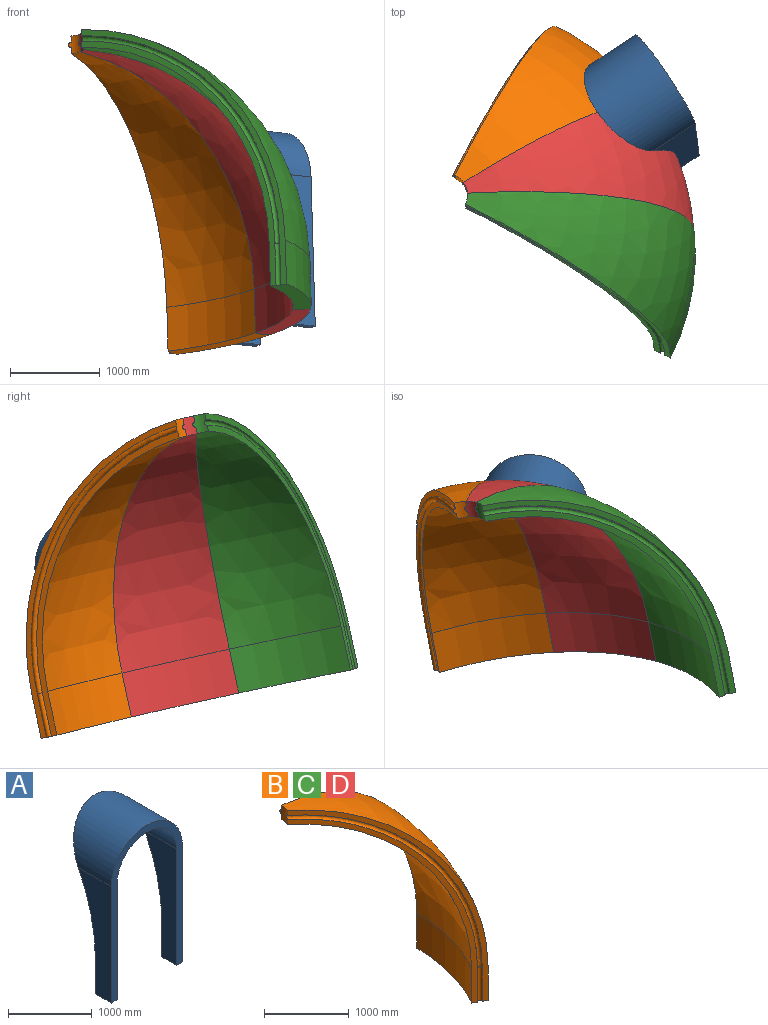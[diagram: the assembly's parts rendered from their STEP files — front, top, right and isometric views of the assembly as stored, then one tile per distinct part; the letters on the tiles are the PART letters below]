
ASSEMBLY  parts=4 mates=7
PART A: 12 faces, bbox 1350.7x951.5x2300 mm
  f0: plane 267.51x100mm, normal (0,0,-1), area 25677.6mm2, adj f1,f7,f8,f9
  f1: plane 1700x533.57mm, normal (1,0,0), area 531535.4mm2, adj f0,f2,f8,f9,f11
  f2: cylinder r=500mm len=1000mm, axis (0,-1,0), area 1103442.8mm2, adj f1,f3,f8,f11
  f3: plane 1700x533.57mm, normal (-1,0,0), area 531535.4mm2, adj f2,f4,f8,f10,f11
  f4: plane 267.51x100mm, normal (0,0,-1), area 25677.6mm2, adj f3,f5,f8,f10
  f5: plane 1700x556.93mm, normal (1,0,0), area 567862.4mm2, adj f4,f6,f8,f10,f11
  f6: cylinder r=600mm len=1200mm, axis (0,-1,0), area 1440019.9mm2, adj f5,f7,f8,f11
  f7: plane 1700x556.93mm, normal (-1,0,0), area 567862.4mm2, adj f0,f6,f8,f9,f11
  f8: plane 2300x1200mm, normal (0,-1,0), area 512787.6mm2, adj f0,f1,f2,f3,f4,f5,f6,f7
  f9: cylinder r=2700mm len=500mm, axis (0,0,-1), area 51074.3mm2, adj f0,f1,f7,f11
  f10: cylinder r=2700mm len=500mm, axis (0,0,-1), area 51074.3mm2, adj f3,f4,f5,f11
  f11: sphere r=2700mm, area 470269.1mm2, adj f1,f2,f3,f5,f6,f7,f9,f10
PART B: 14 faces, bbox 2700x1410x3188.4 mm
  f0: plane 3058.19x2009.8mm, normal (-0.5,-0.87,0), area 296399mm2, adj f4,f7,f8,f9,f12,f13
  f1: bspline ~2635.58x2630.01mm, area 361903.8mm2, adj f2,f6,f11,f13
  f2: plane 3060.29x2320.13mm, normal (0,1,0), area 301979.9mm2, adj f1,f4,f8,f9,f11,f13
  f3: sphere r=2700mm, area 3800637.4mm2, adj f5,f6,f10,f13
  f4: sphere r=2500mm, area 3256088.8mm2, adj f0,f2,f9,f13
  f5: plane 3188.42x2121.78mm, normal (-0.5,-0.87,0), area 310282.6mm2, adj f3,f7,f8,f10,f12,f13
  f6: plane 3188.42x2450.31mm, normal (0,1,0), area 304584.9mm2, adj f1,f3,f8,f10,f11,f13
  f7: bspline ~2634.93x2069.61mm, area 362963.4mm2, adj f0,f5,f12,f13
  f8: plane 1380x534.94mm, normal (0,0,-1), area 272271.4mm2, adj f0,f2,f5,f6,f9,f10,f11,f12
  f9: cylinder r=2500mm len=1250mm, axis (0,0,1), area 654498.5mm2, adj f0,f2,f4,f8
  f10: cylinder r=2700mm len=1350mm, axis (0,0,1), area 706858.3mm2, adj f3,f5,f6,f8
  f11: cylinder r=30mm len=497.18mm, axis (0,0,1), area 46855.3mm2, adj f1,f2,f6,f8
  f12: cylinder r=30mm len=483.61mm, axis (0,0,1), area 45569.8mm2, adj f0,f5,f7,f8
  f13: cylinder r=250mm len=200.93mm, axis (0,0,-1), area 26301.9mm2, adj f0,f1,f2,f3,f4,f5,f6,f7
PART C: same geometry as B
PART D: same geometry as B
PLACE A rot(axis=(-0.07,0.1,0.99),124.3deg) t=(2033.65,871.51,-1621.14)mm
PLACE B rot(axis=(-0.18,0.08,0.98),65deg) t=(-374.98,-720.95,-1351.74)mm
PLACE C rot(axis=(-0.95,-0.09,0.31),12.7deg) t=(-374.98,-720.95,-1351.74)mm
PLACE D rot(axis=(-0.34,0.06,0.94),36deg) t=(-374.98,-720.95,-1351.74)mm
MATE fastened D.f11 <-> B.f12  axis (0.03,-0.21,-0.98) through (1784.48,706.77,-1593.27)mm
MATE fastened B.f0 <-> D.f2  axis (0.56,-0.81,0.19) through (1077.62,655.46,278.77)mm
MATE fastened C.f2 <-> D.f0  axis (-0.07,0.98,-0.21) through (-388.95,-617.11,-862.84)mm
MATE fastened B.f0 <-> D.f2  axis (0.56,-0.81,0.19) through (-388.95,-617.11,-862.84)mm
MATE fastened A.f9 <-> D.f13  axis (-0.03,0.21,0.98) through (-388.95,-617.11,-862.84)mm
MATE fastened D.f2 <-> B.f0  axis (-0.56,0.81,-0.19) through (-388.95,-617.11,-862.84)mm
MATE planar D.f8 <-> A.f4  axis (0.03,-0.21,-0.98) through (2056.11,110.72,-1458.91)mm
